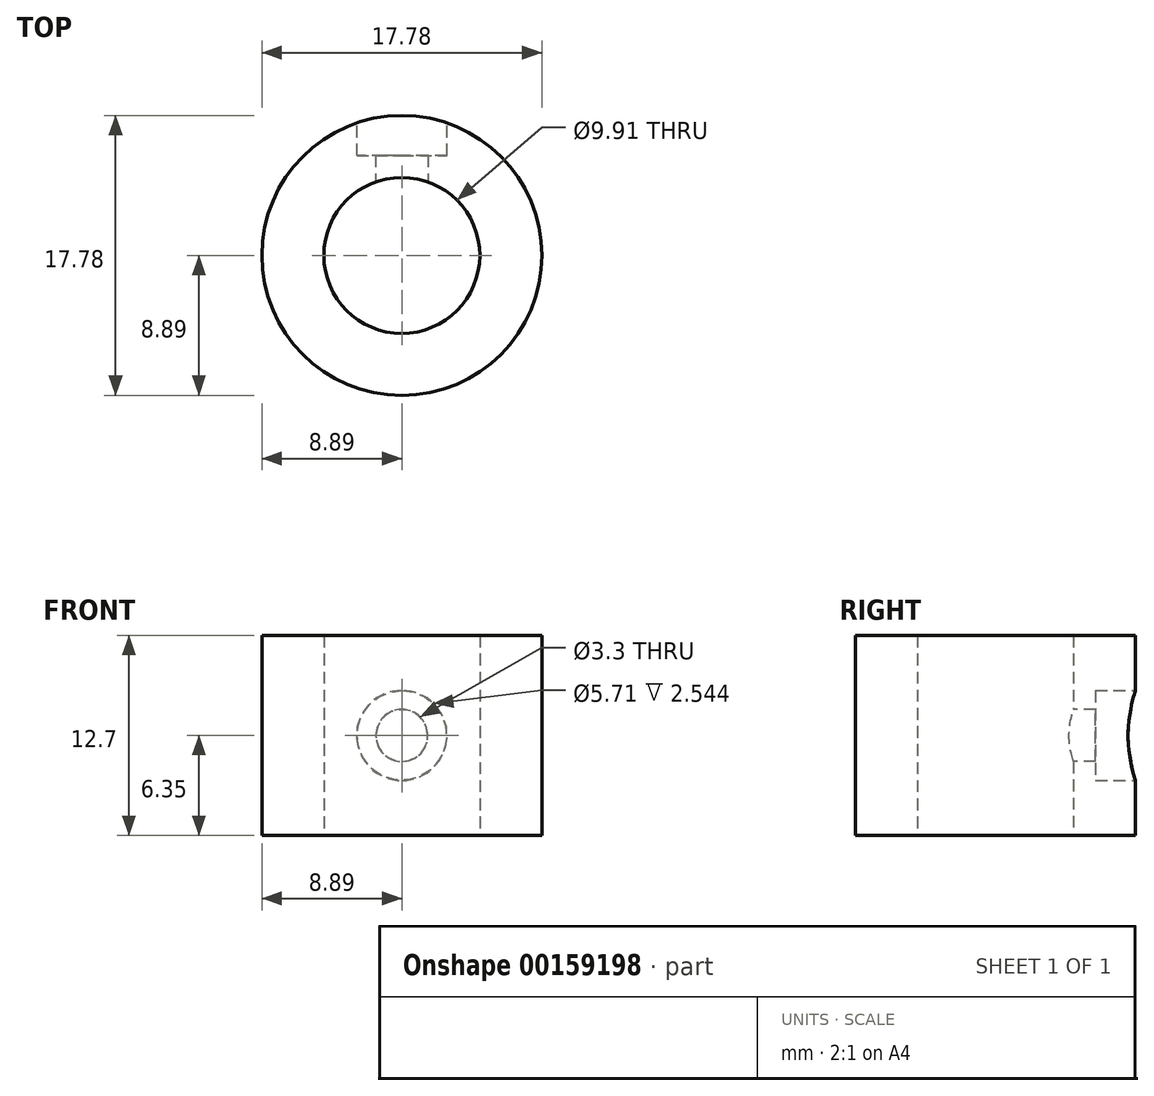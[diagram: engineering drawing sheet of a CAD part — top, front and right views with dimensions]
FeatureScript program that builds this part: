
annotation { "Feature Type Name" : "Feature", "Feature Type Description" : "" }
export const myFeature = defineFeature(function(context is Context, id is Id, definition is map)
    precondition{}
    {
        {
            var Q0;
            Q0=qCreatedBy(makeId("Top.planeOp"),FACE);
            var sketch = newSketch(context, id + "F0", { "sketchPlane" : qUnion([Q0])});
            skCircle(sketch, "E0", {"center": v(0, 0) * mm, "radius": 8.9 * mm});
            skCircle(sketch, "E1", {"center": v(0, 0) * mm, "radius": 4.95 * mm});
            skSolve(sketch);
        }
        {
            var Q0;
            Q0 = qSketchRegion(id + "F0", true);
            extrude(context, id + "F1", {"entities" : qUnion([Q0]), "depth" : 12.7 * mm});
        }
        {
            var Q0;
            Q0=qCreatedBy(makeId("Front.planeOp"),FACE);
            var sketch = newSketch(context, id + "F2", { "sketchPlane" : qUnion([Q0])});
            skLineSegment(sketch, "E2", {"start": v(0, 0) * mm, "end": v(0, 6.35) * mm});
            skCircle(sketch, "E3", {"center": v(0, 6.35) * mm, "radius": 1.65 * mm});
            skSolve(sketch);
        }
        {
            var Q0;
            Q0=makeQuery(id+"F2.imprint","IMPRINT",FACE,{"disambiguationData":[TD([[makeQuery(id+"F2.imprint","IMPRINT",EDGE,{"derivedFrom":sQuery(id+"F2.wireOp",EDGE,"E3")}),1.0]])]});
            extrude(context, id + "F3", {"entities" : qUnion([Q0]), "operationType" : NewBodyOperationType.REMOVE, "oppositeDirection" : true, "depth" : 25.4 * mm});
        }
        {
            var Q0;
            Q0=qCreatedBy(makeId("Front.planeOp"),FACE);
            cPlane(context, id + "F4", {"entities" : qUnion([Q0]), "cplaneType" : CPlaneType.OFFSET, "offset" : 8.9 * mm, "oppositeDirection" : true, "width" : 152.4 * mm, "height" : 152.4 * mm});
        }
        {
            var Q0;
            Q0=qCreatedBy(id+"F4.planeOp",FACE);
            var sketch = newSketch(context, id + "F5", { "sketchPlane" : qUnion([Q0])});
            skCircle(sketch, "E4", {"center": v(0, 6.35) * mm, "radius": 2.86 * mm});
            skSolve(sketch);
        }
        {
            var Q0;
            Q0=makeQuery(id+"F5.imprint","IMPRINT",FACE,{"disambiguationData":[TD([[makeQuery(id+"F5.imprint","IMPRINT",EDGE,{"derivedFrom":sQuery(id+"F5.wireOp",EDGE,"E4")}),1.0]])]});
            extrude(context, id + "F6", {"entities" : qUnion([Q0]), "operationType" : NewBodyOperationType.REMOVE, "depth" : 2.54 * mm});
        }
    });
